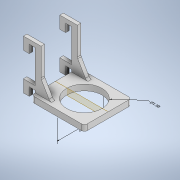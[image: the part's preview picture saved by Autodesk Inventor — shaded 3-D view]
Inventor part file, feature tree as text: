
AUTODESK INVENTOR PART (.ipt)
format: ipt  version: 2021 (Build 250183000, 183)  size: 229,376 bytes
history: native  units: in
note: dims shown in document units (in); Inventor stores cm internally (conversion verified against a paired STEP export)
features: extrude x5, sketch x5, other x3, fillet x3, plane x2, mirror x1
ambient origin geometry x8: Origin, YZ Plane, XZ Plane, XY Plane, X Axis, Y Axis, Z Axis, Center Point
bodies: Solid1 (feature_tree)
feature tree (19):
  other  "Annotations"
  extrude  "Extrusion1"  Depth=0.175in
  plane  "Work Plane1"
  mirror  "Mirror1"
  extrude  "Extrusion4"  Depth=0.25in
  extrude  "Extrusion5"  Depth=0.25in
  fillet  "Fillet1"  Radius=0.15in
  plane  "Work Plane2"
  extrude  "Extrusion6"  Depth=0.525in
  fillet  "Fillet2"  Radius=0.775in
  extrude  "Extrusion7"  Depth=0.25in
  fillet  "Fillet3"  Radius=2.0in
  sketch  "Sketch1"  dims[d1=1.4in d2=0.175in]
  sketch  "Sketch4"  dims[d3=0.175in d4=0.25in]
  sketch  "Sketch5"  dims[d6=0.25in d7=0.25in d11=0.15in d12=0.0in]
  sketch  "Sketch6"  dims[d13=0.525in d14=0.525in d15=0.775in]
  sketch  "Sketch7"  dims[d23=2.25in d24=0.25in d25=2.0in d26=0.0in d27=1.5in d28=1.85in d29=0.0in d30=0.125in d36=-1.0in d37=0.375in d38=60.0deg d39=1.0in d40=0.0in d41=0.125in d42=60.0deg d43=0.375in d44=1.0in d45=0.0in d46=0.125in d31=1.7305in d32=1.5in d33=0.1884in d34=0.2055in d35=2.0in]
  other  "Diameter Dimension 1"
  other  "Linear Dimension 1"
